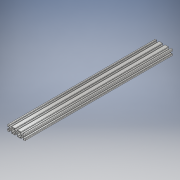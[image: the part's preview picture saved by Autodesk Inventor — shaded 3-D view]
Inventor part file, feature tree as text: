
AUTODESK INVENTOR PART (.ipt)
format: ipt  version: 2019 (Build 230136000, 136)  size: 269,824 bytes
history: native  units: mm
features: extrude x1, sketch x1
ambient origin geometry x8: Origin, YZ Plane, XZ Plane, XY Plane, X Axis, Y Axis, Z Axis, Center Point
bodies: Body1 (feature_tree)
feature tree (2):
  extrude  "Extrusion4"  [1 undecoded]
  sketch  "Sketch1"  dims[d6=500.0mm d7=0.0mm]
note: 1 required parameter value undecoded (feature->parameter linkage not recoverable at this tier; creation-order binding heuristic only, values carry confidence <= 0.55)
